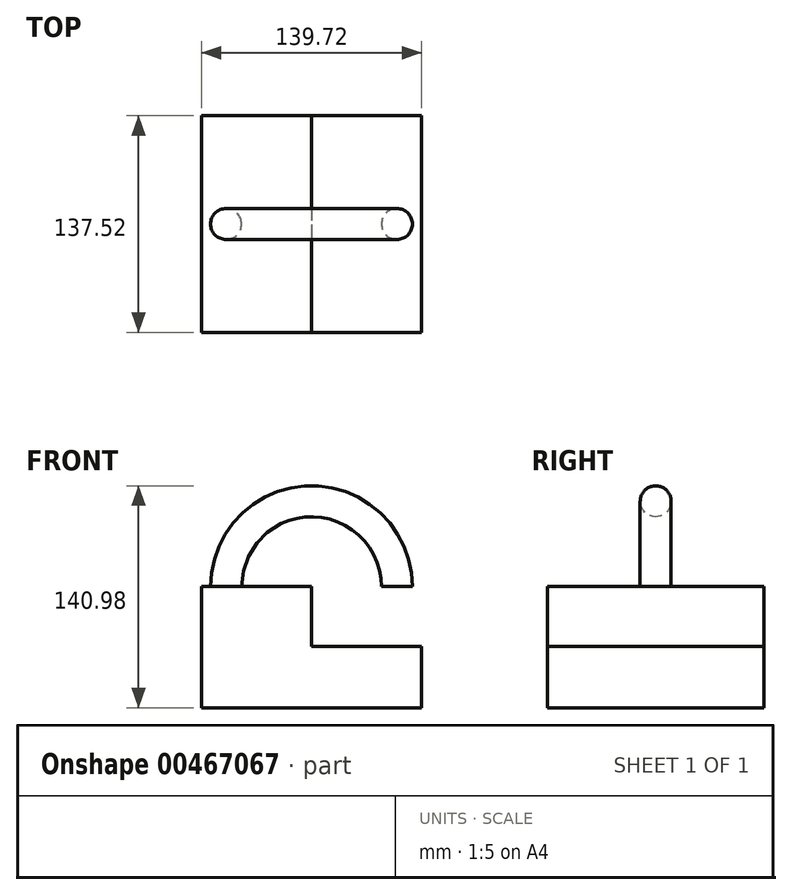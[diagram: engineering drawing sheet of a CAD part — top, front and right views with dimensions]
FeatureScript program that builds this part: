
annotation { "Feature Type Name" : "Feature", "Feature Type Description" : "" }
export const myFeature = defineFeature(function(context is Context, id is Id, definition is map)
    precondition{}
    {
        {
            var Q0;
            Q0=qCreatedBy(makeId("Top.planeOp"),FACE);
            var sketch = newSketch(context, id + "F0", { "sketchPlane" : qUnion([Q0])});
            skLineSegment(sketch, "E0.bottom", {"start": v(69.86, -68.76) * mm, "end": v(-69.86, -68.76) * mm});
            skLineSegment(sketch, "E0.top", {"start": v(69.86, 68.76) * mm, "end": v(-69.86, 68.76) * mm});
            skLineSegment(sketch, "E0.left", {"start": v(69.86, -68.76) * mm, "end": v(69.86, 68.76) * mm});
            skLineSegment(sketch, "E0.right", {"start": v(-69.86, -68.76) * mm, "end": v(-69.86, 68.76) * mm});
            skPoint(sketch, "E0.middle", {"position": v(0, 0) * mm});
            skLineSegment(sketch, "E1", {"start": v(0, 68.76) * mm, "end": v(0, -68.76) * mm});
            skSolve(sketch);
        }
        {
            var Q0;
            Q0=qCreatedBy(makeId("Top.planeOp"),FACE);
            var sketch = newSketch(context, id + "F1", { "sketchPlane" : qUnion([Q0])});
            skCircle(sketch, "E2", {"center": v(54.26, 0) * mm, "radius": 9.82 * mm});
            skSolve(sketch);
        }
        {
            var Q0;
            {var subQ0=sQuery(id+"F0.wireOp",EDGE,"E0.right");Q0=makeQuery(id+"F0.imprint","IMPRINT",FACE,{"disambiguationData":[TD([[makeQuery(id+"F0.imprint","IMPRINT",EDGE,{"derivedFrom":subQ0}),-1.0]])]});}
            var Q1;
            {var subQ0=sQuery(id+"F0.wireOp",EDGE,"E0.left");Q1=makeQuery(id+"F0.imprint","IMPRINT",FACE,{"disambiguationData":[TD([[makeQuery(id+"F0.imprint","IMPRINT",EDGE,{"derivedFrom":subQ0}),1.0]])]});}
            extrude(context, id + "F2", {"entities" : qUnion([Q0, Q1]), "oppositeDirection" : true, "depth" : 76.9 * mm});
        }
        {
            var Q0;
            Q0=makeQuery(id+"F1.imprint","IMPRINT",FACE,{"disambiguationData":[TD([[makeQuery(id+"F1.imprint","IMPRINT",EDGE,{"derivedFrom":sQuery(id+"F1.wireOp",EDGE,"E2")}),1.0]])]});
            var Q1;
            Q1=sQuery(id+"F0.wireOp",EDGE,"E1");
            revolve(context, id + "F3", {"operationType" : NewBodyOperationType.ADD, "entities" : qUnion([Q0]), "axis" : qUnion([Q1]), "revolveType" : RevolveType.FULL});
        }
        {
            var Q0;
            {var subQ0=sQuery(id+"F0.wireOp",EDGE,"E0.left");Q0=makeQuery(id+"F0.imprint","IMPRINT",FACE,{"disambiguationData":[TD([[makeQuery(id+"F0.imprint","IMPRINT",EDGE,{"derivedFrom":subQ0}),1.0]])]});}
            extrude(context, id + "F4", {"entities" : qUnion([Q0]), "operationType" : NewBodyOperationType.ADD, "oppositeDirection" : true, "depth" : 25.4 * mm});
        }
        {
            var Q0;
            {var subQ0=sQuery(id+"F0.wireOp",EDGE,"E0.left");Q0=makeQuery(id+"F0.imprint","IMPRINT",FACE,{"disambiguationData":[TD([[makeQuery(id+"F0.imprint","IMPRINT",EDGE,{"derivedFrom":subQ0}),1.0]])]});}
            extrude(context, id + "F5", {"entities" : qUnion([Q0]), "operationType" : NewBodyOperationType.REMOVE, "oppositeDirection" : true, "depth" : 38.1 * mm});
        }
    });
